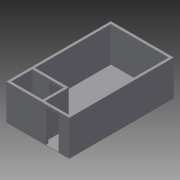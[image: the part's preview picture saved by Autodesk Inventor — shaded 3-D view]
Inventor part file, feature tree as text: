
AUTODESK INVENTOR PART (.ipt)
format: ipt  version: 2013 SP2 (Build 170200200, 200)  size: 126,464 bytes
history: native  units: in
note: dims shown in document units (in); Inventor stores cm internally (conversion verified against a paired STEP export)
features: extrude x3, sketch x3
ambient origin geometry x8: Origin, YZ Plane, XZ Plane, XY Plane, X Axis, Y Axis, Z Axis, Center Point
bodies: Solid1 (feature_tree)
feature tree (6):
  extrude  "Extrusion1"  Depth=256.0in
  extrude  "Extrusion2"  Depth=6.0in
  extrude  "Extrusion3"  Depth=37.0in
  sketch  "Sketch1"  dims[d0=154.0in d2=256.0in]
  sketch  "Sketch2"  dims[d3=6.0in d4=6.0in]
  sketch  "Sketch3"  dims[d5=6.0in d6=6.0in d10=37.0in d11=20.0in d12=31.0in d13=66.0in d14=256.0in d15=37.0in d16=6.0in d17=6.0in d19=58.0in d20=6.0in d21=30.0in d22=59.0in d25=47.0in d26=86.0in d27=0.0in d28=1.0in d29=0.0in d30=6.0in d31=0.0in]
